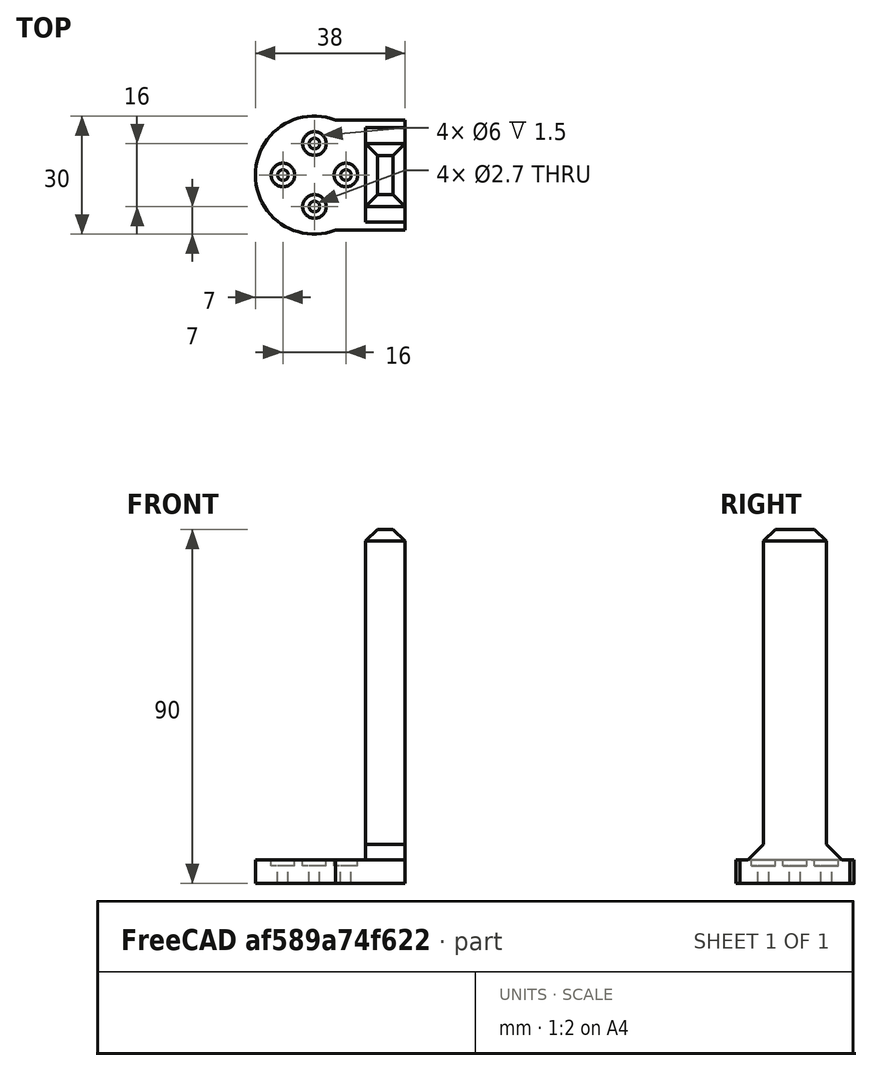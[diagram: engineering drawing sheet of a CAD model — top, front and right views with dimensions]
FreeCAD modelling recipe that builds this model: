
FCSTD DOCUMENT  (FreeCAD 0.15R4671 (Git))
Label: straight_finger
License: All rights reserved
LicenseURL: http://en.wikipedia.org/wiki/All_rights_reserved
objects: Part::Cylinder×9, Part::MultiFuse×3, Part::Chamfer×3, Part::Box×2, Part::Cut×2
note: 19 computed .brp shape members not serialized (recipe doc carries the construction recipe); baked Part::Feature solids carry a one-line shape summary decoded from their .brp

FEATURE [Part::Cylinder] Cylinder
  Angle = 360
  Height = 10
  Placement = pos=(0,-8,-3) rot=(0,0,1;0rad)
  Radius = 1.35
FEATURE [Part::Cylinder] Cylinder001
  Angle = 360
  Height = 10
  Placement = pos=(-8,0,-3) rot=(0,0,1;0rad)
  Radius = 1.35
FEATURE [Part::Cylinder] Cylinder002
  Angle = 360
  Height = 10
  Placement = pos=(8,0,-3) rot=(0,0,1;0rad)
  Radius = 1.35
FEATURE [Part::Cylinder] Cylinder003
  Angle = 360
  Height = 10
  Placement = pos=(0,8,-3) rot=(0,0,1;0rad)
  Radius = 1.35
FEATURE [Part::Cylinder] Cylinder004
  Angle = 360
  Height = 6
  Radius = 15
FEATURE [Part::Box] Box001  label="Cube001"
  Height = 6
  Length = 23
  Placement = pos=(0,-14,0) rot=(0,0,1;0rad)
  Width = 28
FEATURE [Part::MultiFuse] Fusion
  Placement = pos=(0,0,1) rot=(0,0,1;0rad)
  Shapes = -> [Cylinder,Cylinder001,Cylinder002,Cylinder003]
FEATURE [Part::Box] Box  label="Cube"
  Height = 90
  Length = 10
  Placement = pos=(13,-8,0) rot=(0,0,1;0rad)
  Width = 16
FEATURE [Part::MultiFuse] Fusion001
  Shapes = -> [Box,Cylinder004,Box001]
FEATURE [Part::Cut] Cut
  Base = -> Fusion001
  Tool = -> Fusion
FEATURE [Part::Chamfer] Chamfer
  Base = -> Cut
  Edges = 1 edges r=4: [Edge11]
FEATURE [Part::Chamfer] Chamfer001
  Base = -> Chamfer
  Edges = 1 edges r=4: [Edge20]
FEATURE [Part::Chamfer] Chamfer002
  Base = -> Chamfer001
  Edges = 4 edges r=3: [Edge3,Edge13,Edge16,Edge17]
FEATURE [Part::Cylinder] Cylinder005
  Angle = 360
  Height = 10
  Placement = pos=(0,-8,-3) rot=(0,0,1;0rad)
  Radius = 3
FEATURE [Part::Cylinder] Cylinder006
  Angle = 360
  Height = 10
  Placement = pos=(-8,0,-3) rot=(0,0,1;0rad)
  Radius = 3
FEATURE [Part::Cylinder] Cylinder007
  Angle = 360
  Height = 10
  Placement = pos=(8,0,-3) rot=(0,0,1;0rad)
  Radius = 3
FEATURE [Part::Cylinder] Cylinder008
  Angle = 360
  Height = 10
  Placement = pos=(0,8,-3) rot=(0,0,1;0rad)
  Radius = 3
FEATURE [Part::MultiFuse] Fusion002
  Placement = pos=(0,0,7.5) rot=(0,0,1;0rad)
  Shapes = -> [Cylinder005,Cylinder006,Cylinder007,Cylinder008]
FEATURE [Part::Cut] Cut001
  Base = -> Chamfer002
  Tool = -> Fusion002
